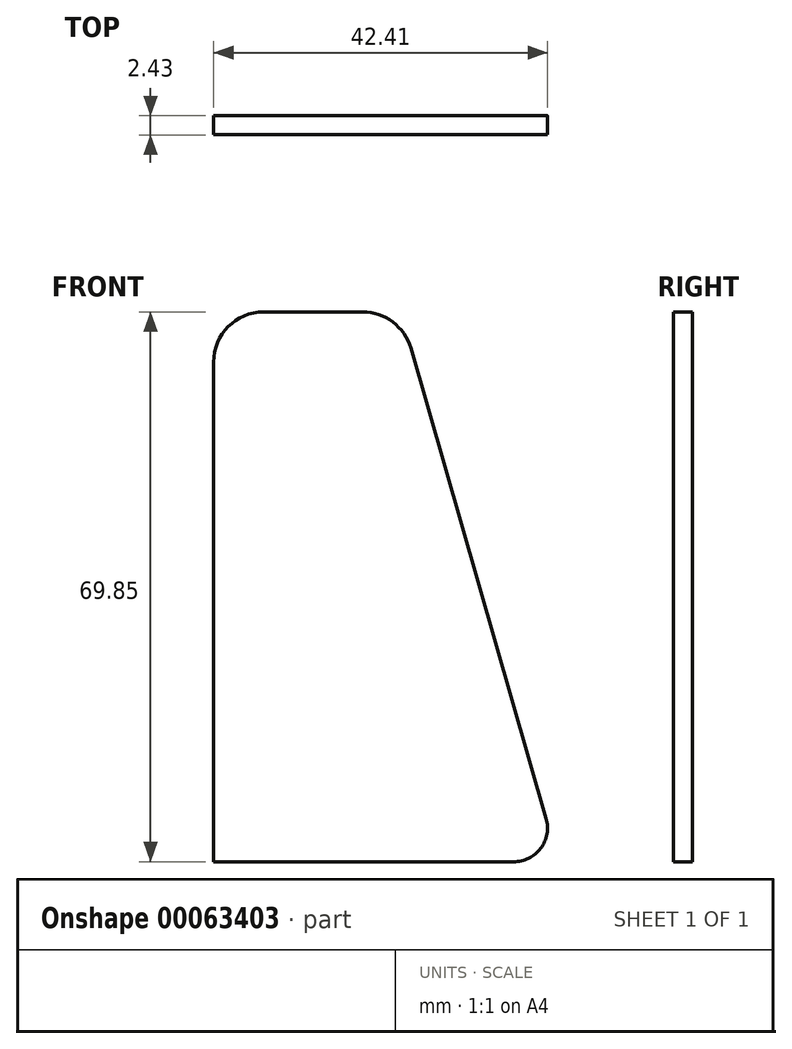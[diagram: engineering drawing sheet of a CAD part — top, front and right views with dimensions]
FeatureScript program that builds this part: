
annotation { "Feature Type Name" : "Feature", "Feature Type Description" : "" }
export const myFeature = defineFeature(function(context is Context, id is Id, definition is map)
    precondition{}
    {
        {
            var Q0;
            Q0=qCreatedBy(makeId("Front.planeOp"),FACE);
            var sketch = newSketch(context, id + "F0", { "sketchPlane" : qUnion([Q0])});
            skLineSegment(sketch, "E0", {"start": v(-38.32, -21.1) * mm, "end": v(-38.32, 42.4) * mm});
            skLineSegment(sketch, "E1", {"start": v(-31.97, 48.75) * mm, "end": v(-19.38, 48.75) * mm});
            skLineSegment(sketch, "E2", {"start": v(-13.28, 44.15) * mm, "end": v(3.93, -15.6) * mm});
            skLineSegment(sketch, "E3", {"start": v(-0.22, -21.1) * mm, "end": v(-38.32, -21.1) * mm});
            skPoint(sketch, "E4.visualSharp", {"position": v(-38.32, 48.75) * mm});
            skArc(sketch, "E4.filletArc", {"start": v(-31.97, 48.75) * mm, "mid": v(-36.46, 46.89) * mm, "end": v(-38.32, 42.4) * mm});
            skPoint(sketch, "E5.visualSharp", {"position": v(-14.6, 48.75) * mm});
            skArc(sketch, "E5.filletArc", {"start": v(-13.28, 44.15) * mm, "mid": v(-15.56, 47.47) * mm, "end": v(-19.38, 48.75) * mm});
            skPoint(sketch, "E6.visualSharp", {"position": v(5.51, -21.1) * mm});
            skArc(sketch, "E6.filletArc", {"start": v(-0.22, -21.1) * mm, "mid": v(3.23, -19.38) * mm, "end": v(3.93, -15.6) * mm});
            skSolve(sketch);
        }
        {
            var Q0;
            Q0=makeQuery(id+"F0.imprint","IMPRINT",FACE,{"disambiguationData":[TD([[makeQuery(id+"F0.imprint","IMPRINT",EDGE,{"derivedFrom":sQuery(id+"F0.wireOp",EDGE,"E0")}),-1.0]])]});
            extrude(context, id + "F1", {"entities" : qUnion([Q0]), "depth" : 2.43 * mm});
        }
    });
